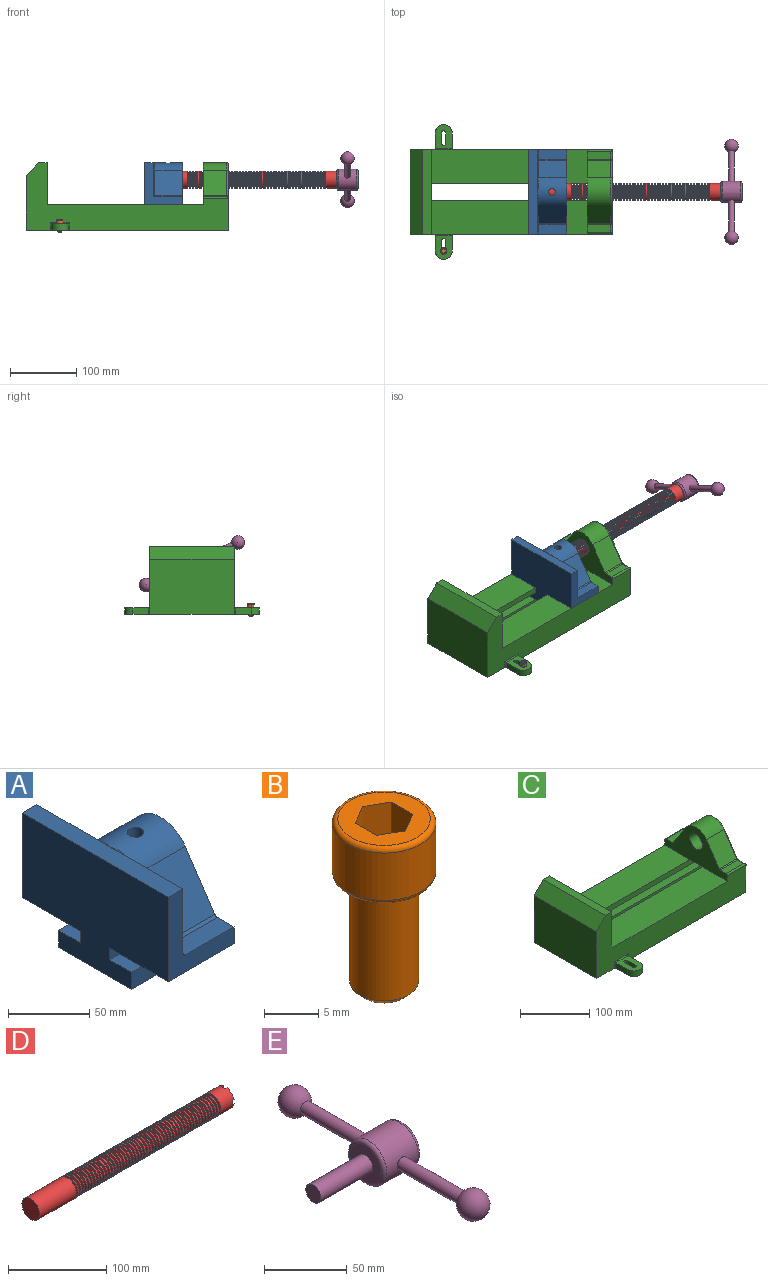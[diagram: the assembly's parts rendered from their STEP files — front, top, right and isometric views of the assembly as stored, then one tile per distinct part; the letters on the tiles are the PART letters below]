
ASSEMBLY  parts=5 mates=5
PART A: 36 faces, bbox 57.2x127x89 mm
  f0: plane 57.15x50.8mm, normal (0,0,-1), area 2903.2mm2, adj f6,f9,f10,f23
  f1: cylinder r=12.7mm len=44.45mm, axis (1,0,0), area 3464.3mm2, adj f6,f15,f16
  f2: plane 41.91x14.52mm, normal (0,0,1), area 608.5mm2, adj f6,f11,f24,f25
  f3: plane 51.86x48.26mm, normal (1,0,0), area 1495.7mm2, adj f8,f10,f31,f33,f35
  f4: plane 51.86x48.26mm, normal (1,0,0), area 1495.7mm2, adj f8,f11,f24,f28,f29
  f5: plane 57.15x50.8mm, normal (0,0,-1), area 2903.2mm2, adj f6,f9,f11,f22
  f6: plane 127x85.09mm, normal (1,0,0), area 5190.6mm2, adj f0,f1,f2,f5,f7,f10,f11,f12
  f7: plane 41.91x14.52mm, normal (0,0,1), area 608.5mm2, adj f6,f10,f30,f31
  f8: plane 127x12.7mm, normal (0,0,1), area 1612.9mm2, adj f3,f4,f9,f10,f11,f26,f34
  f9: plane 127x85.09mm, normal (-1,0,0), area 9096.8mm2, adj f0,f5,f8,f10,f11,f17,f18,f19
  f10: plane 63.5x57.15mm, normal (0,-1,0), area 1372.3mm2, adj f0,f3,f6,f7,f8,f9,f31
  f11: plane 63.5x57.15mm, normal (0,1,0), area 1372.3mm2, adj f2,f4,f5,f6,f8,f9,f24
  f12: plane 41.91x38.43mm, normal (0,-0.83,0.56), area 1939.2mm2, adj f6,f13,f30,f33
  f13: cylinder r=25.4mm len=44.45mm, axis (1,0,0), area 2026.5mm2, adj f6,f12,f14,f16,f26,f28,f34,f35
  f14: plane 41.91x38.43mm, normal (0,0.83,0.56), area 1939.2mm2, adj f6,f13,f25,f29
  f15: plane 25.4x25.4mm, normal (1,0,0), area 506.7mm2, adj f1
  f16: cylinder r=5.08mm len=13.76mm, axis (0,0,1), area 414mm2, adj f1,f13
  f17: plane 57.15x19.05mm, normal (0,0,1), area 1088.7mm2, adj f6,f9,f18,f23
  f18: plane 57.15x12.7mm, normal (0,-1,0), area 725.8mm2, adj f6,f9,f17,f19
  f19: plane 63.5x57.15mm, normal (0,0,-1), area 3629mm2, adj f6,f9,f18,f20
  f20: plane 57.15x12.7mm, normal (0,1,0), area 725.8mm2, adj f6,f9,f19,f21
  f21: plane 57.15x19.05mm, normal (0,0,1), area 1088.7mm2, adj f6,f9,f20,f22
  f22: plane 57.15x8.89mm, normal (0,1,0), area 508.1mm2, adj f5,f6,f9,f21
  f23: plane 57.15x8.89mm, normal (0,-1,0), area 508.1mm2, adj f0,f6,f9,f17
  f24: cylinder r=2.54mm len=14.52mm, axis (0,-1,0), area 57.9mm2, adj f2,f4,f11,f27
  f25: cylinder r=2.54mm len=41.91mm, axis (1,0,0), area 104.3mm2, adj f2,f6,f14,f27
  f26: bspline ~12.24x2.8mm, area 20.9mm2, adj f8,f13,f28
  f27: sphere r=2.54mm, area 6.3mm2, adj f24,f25,f29
  f28: torus R=27.94mm, axis (1,0,0), area 57.8mm2, adj f4,f13,f26,f29
  f29: cylinder r=2.54mm len=39.84mm, axis (0,-0.56,0.83), area 184.6mm2, adj f4,f14,f27,f28
  f30: cylinder r=2.54mm len=41.91mm, axis (1,0,0), area 104.3mm2, adj f6,f7,f12,f32
  f31: cylinder r=2.54mm len=14.52mm, axis (0,-1,0), area 57.9mm2, adj f3,f7,f10,f32
  f32: sphere r=2.54mm, area 6.3mm2, adj f30,f31,f33
  f33: cylinder r=2.54mm len=39.84mm, axis (0,-0.56,-0.83), area 184.6mm2, adj f3,f12,f32,f35
  f34: bspline ~12.24x2.8mm, area 20.9mm2, adj f8,f13,f35
  f35: torus R=27.94mm, axis (1,0,0), area 57.8mm2, adj f3,f13,f33,f34
PART B: 15 faces, bbox 10.3x10.3x19.1 mm
  f0: plane 8.51x8.51mm, normal (0,0,1), area 37.2mm2, adj f5,f6,f7,f8,f9,f10,f14
  f1: cylinder r=3.17mm len=11.94mm, axis (0,0,1), area 238.2mm2, adj f4,f12
  f2: plane 4.83x4.83mm, normal (0,0,-1), area 18.3mm2, adj f12
  f3: cylinder r=4.76mm len=9.53mm, axis (0,0,-1), area 159.6mm2, adj f13,f14
  f4: plane 8.51x8.51mm, normal (0,0,-1), area 25.2mm2, adj f1,f13
  f5: plane 4.83x2.38mm, normal (-0.5,-0.87,0), area 13.3mm2, adj f0,f6,f10,f11
  f6: plane 4.83x2.38mm, normal (0.5,-0.87,0), area 13.3mm2, adj f0,f5,f7,f11
  f7: plane 4.83x2.75mm, normal (1,0,0), area 13.3mm2, adj f0,f6,f8,f11
  f8: plane 4.83x2.38mm, normal (0.5,0.87,0), area 13.3mm2, adj f0,f7,f9,f11
  f9: plane 4.83x2.38mm, normal (-0.5,0.87,0), area 13.3mm2, adj f0,f8,f10,f11
  f10: plane 4.83x2.75mm, normal (-1,0,0), area 13.3mm2, adj f0,f5,f9,f11
  f11: plane 5.5x4.76mm, normal (0,0,1), area 19.6mm2, adj f5,f6,f7,f8,f9,f10
  f12: cone r=3.17mm half-angle=45deg, axis (0,0,1), area 18.9mm2, adj f1,f2
  f13: torus R=4.25mm, axis (0,0,1), area 23mm2, adj f3,f4
  f14: torus R=4.25mm, axis (0,0,1), area 23mm2, adj f0,f3
PART C: 61 faces, bbox 304.8x203.2x103.7 mm
  f0: plane 304.8x101.6mm, normal (0,1,0), area 13520.3mm2, adj f3,f4,f5,f6,f7,f8,f9,f16
  f1: plane 304.8x101.6mm, normal (0,-1,0), area 13520.3mm2, adj f2,f3,f5,f6,f7,f8,f9,f16
  f2: plane 234.95x50.8mm, normal (0,0,1), area 11935.5mm2, adj f1,f5,f16,f26
  f3: plane 127x99.06mm, normal (1,0,0), area 7097.5mm2, adj f0,f1,f9,f14,f17,f18,f19,f20
  f4: plane 234.95x50.8mm, normal (0,0,1), area 11935.5mm2, adj f0,f5,f16,f27
  f5: plane 127x101.6mm, normal (1,0,0), area 9516.1mm2, adj f0,f1,f2,f4,f6,f9,f18,f19
  f6: plane 127x12.7mm, normal (0,0,1), area 1612.9mm2, adj f0,f1,f5,f7
  f7: plane 127x19.05mm, normal (-0.71,0,0.71), area 3421.5mm2, adj f0,f1,f6,f8
  f8: plane 127x82.55mm, normal (-1,0,0), area 10483.8mm2, adj f0,f1,f7,f9
  f9: plane 304.8x203.2mm, normal (0,0,-1), area 33298.3mm2, adj f0,f1,f3,f5,f8,f21,f22,f39
  f10: plane 35.56x11.98mm, normal (0,0,1), area 426mm2, adj f16,f28,f29,f30
  f11: plane 38.43x35.56mm, normal (0,0.83,0.56), area 1645.4mm2, adj f12,f16,f29,f32
  f12: cylinder r=25.4mm len=42.19mm, axis (1,0,0), area 1770.2mm2, adj f11,f13,f16,f33
  f13: plane 38.43x35.56mm, normal (0,-0.83,0.56), area 1645.4mm2, adj f12,f16,f34,f35
  f14: cylinder r=12.7mm len=38.1mm, axis (1,0,0), area 3040.2mm2, adj f3,f16
  f15: plane 35.56x11.98mm, normal (0,0,1), area 426mm2, adj f16,f34,f36,f38
  f16: plane 127x63.5mm, normal (-1,0,0), area 4155.5mm2, adj f0,f1,f2,f4,f10,f11,f12,f13
  f17: plane 38.1x25.4mm, normal (0,0,-1), area 967.7mm2, adj f3,f16,f26,f27
  f18: plane 273.05x19.05mm, normal (0,0,-1), area 5201.6mm2, adj f3,f5,f19,f26
  f19: plane 273.05x12.7mm, normal (0,1,0), area 3467.7mm2, adj f3,f5,f18,f20
  f20: plane 273.05x19.05mm, normal (0,0,1), area 5201.6mm2, adj f3,f5,f19,f21
  f21: plane 273.05x16.51mm, normal (0,1,0), area 4508.1mm2, adj f3,f5,f9,f20
  f22: plane 273.05x16.51mm, normal (0,-1,0), area 4508.1mm2, adj f3,f5,f9,f23
  f23: plane 273.05x19.05mm, normal (0,0,1), area 5201.6mm2, adj f3,f5,f22,f24
  f24: plane 273.05x12.7mm, normal (0,-1,0), area 3467.7mm2, adj f3,f5,f23,f25
  f25: plane 273.05x19.05mm, normal (0,0,-1), area 5201.6mm2, adj f3,f5,f24,f27
  f26: plane 273.05x8.89mm, normal (0,1,0), area 2427.4mm2, adj f2,f3,f5,f17,f18
  f27: plane 273.05x8.89mm, normal (0,-1,0), area 2427.4mm2, adj f3,f4,f5,f17,f25
  f28: cylinder r=2.54mm len=38.1mm, axis (1,0,0), area 148.3mm2, adj f0,f10,f16,f30
  f29: cylinder r=2.54mm len=35.56mm, axis (-1,0,0), area 88.5mm2, adj f10,f11,f16,f31
  f30: cylinder r=2.54mm len=14.52mm, axis (0,1,0), area 54.3mm2, adj f3,f10,f28,f31
  f31: torus R=5.08mm, axis (-1,0,0), area 13.5mm2, adj f3,f29,f30,f32
  f32: cylinder r=2.54mm len=39.84mm, axis (0,0.56,-0.83), area 184.6mm2, adj f3,f11,f31,f33
  f33: torus R=22.86mm, axis (-1,0,0), area 191.4mm2, adj f3,f12,f32,f35
  f34: cylinder r=2.54mm len=35.56mm, axis (-1,0,0), area 88.5mm2, adj f13,f15,f16,f37
  f35: cylinder r=2.54mm len=39.84mm, axis (0,0.56,0.83), area 184.6mm2, adj f3,f13,f33,f37
  f36: cylinder r=2.54mm len=38.1mm, axis (-1,0,0), area 148.3mm2, adj f1,f15,f16,f38
  f37: torus R=5.08mm, axis (-1,0,0), area 13.5mm2, adj f3,f34,f35,f38
  f38: cylinder r=2.54mm len=14.52mm, axis (0,1,0), area 54.3mm2, adj f3,f15,f36,f37
  f39: plane 23.88x9.53mm, normal (-1,0,0), area 227.4mm2, adj f9,f45,f46,f60
  f40: plane 23.88x9.53mm, normal (1,0,0), area 227.4mm2, adj f9,f45,f46,f58
  f41: cylinder r=3.3mm len=9.53mm, axis (0,0,-1), area 98.8mm2, adj f9,f42,f44,f46
  f42: plane 15.62x9.53mm, normal (-1,0,0), area 148.8mm2, adj f9,f41,f43,f46
  f43: cylinder r=3.3mm len=9.53mm, axis (0,0,-1), area 98.8mm2, adj f9,f42,f44,f46
  f44: plane 15.62x9.53mm, normal (1,0,0), area 148.8mm2, adj f9,f41,f43,f46
  f45: cylinder r=12.7mm len=25.4mm, axis (0,0,-1), area 380mm2, adj f9,f39,f40,f46
  f46: plane 36.58x25.4mm, normal (0,0,1), area 722.4mm2, adj f39,f40,f41,f42,f43,f44,f45,f59
  f47: plane 23.88x9.53mm, normal (-1,0,0), area 227.4mm2, adj f9,f53,f54,f56
  f48: plane 23.88x9.53mm, normal (1,0,0), area 227.4mm2, adj f9,f53,f54,f55
  f49: cylinder r=3.3mm len=9.53mm, axis (0,0,-1), area 98.8mm2, adj f9,f50,f52,f54
  f50: plane 15.62x9.53mm, normal (-1,0,0), area 148.8mm2, adj f9,f49,f51,f54
  f51: cylinder r=3.3mm len=9.53mm, axis (0,0,-1), area 98.8mm2, adj f9,f50,f52,f54
  f52: plane 15.62x9.53mm, normal (1,0,0), area 148.8mm2, adj f9,f49,f51,f54
  f53: cylinder r=12.7mm len=25.4mm, axis (0,0,-1), area 380mm2, adj f9,f47,f48,f54
  f54: plane 36.58x25.4mm, normal (0,0,1), area 722.4mm2, adj f47,f48,f49,f50,f51,f52,f53,f57
  f55: cylinder r=1.52mm len=11.05mm, axis (0,0,-1), area 24.1mm2, adj f0,f9,f48,f57
  f56: cylinder r=1.52mm len=11.05mm, axis (0,0,1), area 24.1mm2, adj f0,f9,f47,f57
  f57: cylinder r=1.52mm len=28.45mm, axis (1,0,0), area 63.5mm2, adj f0,f54,f55,f56
  f58: cylinder r=1.52mm len=11.05mm, axis (0,0,1), area 24.1mm2, adj f1,f9,f40,f59
  f59: cylinder r=1.52mm len=28.45mm, axis (-1,0,0), area 63.5mm2, adj f1,f46,f58,f60
  f60: cylinder r=1.52mm len=11.05mm, axis (0,0,-1), area 24.1mm2, adj f1,f9,f39,f59
PART D: 220 faces, bbox 279.4x25.4x25.4 mm
  f0: cylinder r=12.7mm len=25.4mm, axis (-1,0,0), area 1468.2mm2, adj f1,f2,f3,f5,f7,f208,f209,f210
  f1: plane 9.9x9.9mm, normal (1,0,0), area 62.3mm2, adj f0,f4,f213,f216
  f2: plane 9.9x9.9mm, normal (1,0,0), area 62.3mm2, adj f0,f4,f210,f218
  f3: plane 9.9x9.9mm, normal (1,0,0), area 62.3mm2, adj f0,f4,f209,f212
  f4: cylinder r=6.35mm len=25.4mm, axis (1,0,0), area 960.3mm2, adj f1,f2,f3,f5,f6,f208,f209,f210
  f5: plane 9.9x9.9mm, normal (1,0,0), area 62.3mm2, adj f0,f4,f215,f217
  f6: plane 12.7x12.7mm, normal (1,0,0), area 126.7mm2, adj f4
  f7: cone r=12.7mm half-angle=76deg, axis (1,0,0), area 188mm2, adj f0,f9
  f8: cone r=10.16mm half-angle=76deg, axis (-1,0,0), area 188mm2, adj f9,f10
  f9: cylinder r=10.16mm len=20.32mm, axis (1,0,0), area 81.1mm2, adj f7,f8
  f10: cylinder r=12.7mm len=25.4mm, axis (-1,0,0), area 131.7mm2, adj f8,f11
  f11: cone r=12.7mm half-angle=76deg, axis (1,0,0), area 188mm2, adj f10,f13
  f12: cone r=10.16mm half-angle=76deg, axis (-1,0,0), area 188mm2, adj f13,f14
  f13: cylinder r=10.16mm len=20.32mm, axis (1,0,0), area 81.1mm2, adj f11,f12
  f14: cylinder r=12.7mm len=25.4mm, axis (-1,0,0), area 131.7mm2, adj f12,f15
  f15: cone r=12.7mm half-angle=76deg, axis (1,0,0), area 188mm2, adj f14,f17
  f16: cone r=10.16mm half-angle=76deg, axis (-1,0,0), area 188mm2, adj f17,f18
  f17: cylinder r=10.16mm len=20.32mm, axis (1,0,0), area 81.1mm2, adj f15,f16
  f18: cylinder r=12.7mm len=25.4mm, axis (-1,0,0), area 131.7mm2, adj f16,f19
  f19: cone r=12.7mm half-angle=76deg, axis (1,0,0), area 188mm2, adj f18,f21
  f20: cone r=10.16mm half-angle=76deg, axis (-1,0,0), area 188mm2, adj f21,f22
  f21: cylinder r=10.16mm len=20.32mm, axis (1,0,0), area 81.1mm2, adj f19,f20
  f22: cylinder r=12.7mm len=25.4mm, axis (-1,0,0), area 131.7mm2, adj f20,f23
  f23: cone r=12.7mm half-angle=76deg, axis (1,0,0), area 188mm2, adj f22,f25
  f24: cone r=10.16mm half-angle=76deg, axis (-1,0,0), area 188mm2, adj f25,f26
  f25: cylinder r=10.16mm len=20.32mm, axis (1,0,0), area 81.1mm2, adj f23,f24
  f26: cylinder r=12.7mm len=25.4mm, axis (-1,0,0), area 131.7mm2, adj f24,f27
  f27: cone r=12.7mm half-angle=76deg, axis (1,0,0), area 188mm2, adj f26,f29
  f28: cone r=10.16mm half-angle=76deg, axis (-1,0,0), area 188mm2, adj f29,f30
  f29: cylinder r=10.16mm len=20.32mm, axis (1,0,0), area 81.1mm2, adj f27,f28
  f30: cylinder r=12.7mm len=25.4mm, axis (-1,0,0), area 131.7mm2, adj f28,f31
  f31: cone r=12.7mm half-angle=76deg, axis (1,0,0), area 188mm2, adj f30,f33
  f32: cone r=10.16mm half-angle=76deg, axis (-1,0,0), area 188mm2, adj f33,f34
  f33: cylinder r=10.16mm len=20.32mm, axis (1,0,0), area 81.1mm2, adj f31,f32
  f34: cylinder r=12.7mm len=25.4mm, axis (-1,0,0), area 131.7mm2, adj f32,f35
  f35: cone r=12.7mm half-angle=76deg, axis (1,0,0), area 188mm2, adj f34,f37
  f36: cone r=10.16mm half-angle=76deg, axis (-1,0,0), area 188mm2, adj f37,f38
  f37: cylinder r=10.16mm len=20.32mm, axis (1,0,0), area 81.1mm2, adj f35,f36
  f38: cylinder r=12.7mm len=25.4mm, axis (-1,0,0), area 131.7mm2, adj f36,f39
  f39: cone r=12.7mm half-angle=76deg, axis (1,0,0), area 188mm2, adj f38,f41
  f40: cone r=10.16mm half-angle=76deg, axis (-1,0,0), area 188mm2, adj f41,f42
  f41: cylinder r=10.16mm len=20.32mm, axis (1,0,0), area 81.1mm2, adj f39,f40
  f42: cylinder r=12.7mm len=25.4mm, axis (-1,0,0), area 131.7mm2, adj f40,f43
  f43: cone r=12.7mm half-angle=76deg, axis (1,0,0), area 188mm2, adj f42,f45
  f44: cone r=10.16mm half-angle=76deg, axis (-1,0,0), area 188mm2, adj f45,f46
  f45: cylinder r=10.16mm len=20.32mm, axis (1,0,0), area 81.1mm2, adj f43,f44
  f46: cylinder r=12.7mm len=25.4mm, axis (-1,0,0), area 131.7mm2, adj f44,f47
  f47: cone r=12.7mm half-angle=76deg, axis (1,0,0), area 188mm2, adj f46,f49
  f48: cone r=10.16mm half-angle=76deg, axis (-1,0,0), area 188mm2, adj f49,f50
  f49: cylinder r=10.16mm len=20.32mm, axis (1,0,0), area 81.1mm2, adj f47,f48
  f50: cylinder r=12.7mm len=25.4mm, axis (-1,0,0), area 131.7mm2, adj f48,f51
  f51: cone r=12.7mm half-angle=76deg, axis (1,0,0), area 188mm2, adj f50,f53
  f52: cone r=10.16mm half-angle=76deg, axis (-1,0,0), area 188mm2, adj f53,f54
  f53: cylinder r=10.16mm len=20.32mm, axis (1,0,0), area 81.1mm2, adj f51,f52
  f54: cylinder r=12.7mm len=25.4mm, axis (-1,0,0), area 131.7mm2, adj f52,f55
  f55: cone r=12.7mm half-angle=76deg, axis (1,0,0), area 188mm2, adj f54,f57
  f56: cone r=10.16mm half-angle=76deg, axis (-1,0,0), area 188mm2, adj f57,f58
  f57: cylinder r=10.16mm len=20.32mm, axis (1,0,0), area 81.1mm2, adj f55,f56
  f58: cylinder r=12.7mm len=25.4mm, axis (-1,0,0), area 131.7mm2, adj f56,f59
  f59: cone r=12.7mm half-angle=76deg, axis (1,0,0), area 188mm2, adj f58,f61
  f60: cone r=10.16mm half-angle=76deg, axis (-1,0,0), area 188mm2, adj f61,f62
  f61: cylinder r=10.16mm len=20.32mm, axis (1,0,0), area 81.1mm2, adj f59,f60
  f62: cylinder r=12.7mm len=25.4mm, axis (-1,0,0), area 131.7mm2, adj f60,f63
  f63: cone r=12.7mm half-angle=76deg, axis (1,0,0), area 188mm2, adj f62,f65
  f64: cone r=10.16mm half-angle=76deg, axis (-1,0,0), area 188mm2, adj f65,f66
  f65: cylinder r=10.16mm len=20.32mm, axis (1,0,0), area 81.1mm2, adj f63,f64
  f66: cylinder r=12.7mm len=25.4mm, axis (-1,0,0), area 131.7mm2, adj f64,f67
  f67: cone r=12.7mm half-angle=76deg, axis (1,0,0), area 188mm2, adj f66,f69
  f68: cone r=10.16mm half-angle=76deg, axis (-1,0,0), area 188mm2, adj f69,f70
  f69: cylinder r=10.16mm len=20.32mm, axis (1,0,0), area 81.1mm2, adj f67,f68
  f70: cylinder r=12.7mm len=25.4mm, axis (-1,0,0), area 131.7mm2, adj f68,f71
  f71: cone r=12.7mm half-angle=76deg, axis (1,0,0), area 188mm2, adj f70,f73
  f72: cone r=10.16mm half-angle=76deg, axis (-1,0,0), area 188mm2, adj f73,f74
  f73: cylinder r=10.16mm len=20.32mm, axis (1,0,0), area 81.1mm2, adj f71,f72
  f74: cylinder r=12.7mm len=25.4mm, axis (-1,0,0), area 131.7mm2, adj f72,f75
  f75: cone r=12.7mm half-angle=76deg, axis (1,0,0), area 188mm2, adj f74,f77
  f76: cone r=10.16mm half-angle=76deg, axis (-1,0,0), area 188mm2, adj f77,f78
  f77: cylinder r=10.16mm len=20.32mm, axis (1,0,0), area 81.1mm2, adj f75,f76
  f78: cylinder r=12.7mm len=25.4mm, axis (-1,0,0), area 131.7mm2, adj f76,f79
  f79: cone r=12.7mm half-angle=76deg, axis (1,0,0), area 188mm2, adj f78,f81
  f80: cone r=10.16mm half-angle=76deg, axis (-1,0,0), area 188mm2, adj f81,f82
  f81: cylinder r=10.16mm len=20.32mm, axis (1,0,0), area 81.1mm2, adj f79,f80
  f82: cylinder r=12.7mm len=25.4mm, axis (-1,0,0), area 131.7mm2, adj f80,f83
  f83: cone r=12.7mm half-angle=76deg, axis (1,0,0), area 188mm2, adj f82,f85
  f84: cone r=10.16mm half-angle=76deg, axis (-1,0,0), area 188mm2, adj f85,f86
  f85: cylinder r=10.16mm len=20.32mm, axis (1,0,0), area 81.1mm2, adj f83,f84
  f86: cylinder r=12.7mm len=25.4mm, axis (-1,0,0), area 131.7mm2, adj f84,f87
  f87: cone r=12.7mm half-angle=76deg, axis (1,0,0), area 188mm2, adj f86,f89
  f88: cone r=10.16mm half-angle=76deg, axis (-1,0,0), area 188mm2, adj f89,f90
  f89: cylinder r=10.16mm len=20.32mm, axis (1,0,0), area 81.1mm2, adj f87,f88
  f90: cylinder r=12.7mm len=25.4mm, axis (-1,0,0), area 131.7mm2, adj f88,f91
  f91: cone r=12.7mm half-angle=76deg, axis (1,0,0), area 188mm2, adj f90,f93
  f92: cone r=10.16mm half-angle=76deg, axis (-1,0,0), area 188mm2, adj f93,f94
  f93: cylinder r=10.16mm len=20.32mm, axis (1,0,0), area 81.1mm2, adj f91,f92
  f94: cylinder r=12.7mm len=25.4mm, axis (-1,0,0), area 131.7mm2, adj f92,f95
  f95: cone r=12.7mm half-angle=76deg, axis (1,0,0), area 188mm2, adj f94,f97
  f96: cone r=10.16mm half-angle=76deg, axis (-1,0,0), area 188mm2, adj f97,f98
  f97: cylinder r=10.16mm len=20.32mm, axis (1,0,0), area 81.1mm2, adj f95,f96
  f98: cylinder r=12.7mm len=25.4mm, axis (-1,0,0), area 131.7mm2, adj f96,f99
  f99: cone r=12.7mm half-angle=76deg, axis (1,0,0), area 188mm2, adj f98,f101
  f100: cone r=10.16mm half-angle=76deg, axis (-1,0,0), area 188mm2, adj f101,f102
  f101: cylinder r=10.16mm len=20.32mm, axis (1,0,0), area 81.1mm2, adj f99,f100
  f102: cylinder r=12.7mm len=25.4mm, axis (-1,0,0), area 131.7mm2, adj f100,f103
  f103: cone r=12.7mm half-angle=76deg, axis (1,0,0), area 188mm2, adj f102,f105
  f104: cone r=10.16mm half-angle=76deg, axis (-1,0,0), area 188mm2, adj f105,f106
  f105: cylinder r=10.16mm len=20.32mm, axis (1,0,0), area 81.1mm2, adj f103,f104
  f106: cylinder r=12.7mm len=25.4mm, axis (-1,0,0), area 131.7mm2, adj f104,f107
  f107: cone r=12.7mm half-angle=76deg, axis (1,0,0), area 188mm2, adj f106,f109
  f108: cone r=10.16mm half-angle=76deg, axis (-1,0,0), area 188mm2, adj f109,f110
  f109: cylinder r=10.16mm len=20.32mm, axis (1,0,0), area 81.1mm2, adj f107,f108
  f110: cylinder r=12.7mm len=25.4mm, axis (-1,0,0), area 131.7mm2, adj f108,f111
  f111: cone r=12.7mm half-angle=76deg, axis (1,0,0), area 188mm2, adj f110,f113
  f112: cone r=10.16mm half-angle=76deg, axis (-1,0,0), area 188mm2, adj f113,f114
  f113: cylinder r=10.16mm len=20.32mm, axis (1,0,0), area 81.1mm2, adj f111,f112
  f114: cylinder r=12.7mm len=25.4mm, axis (-1,0,0), area 131.7mm2, adj f112,f115
  f115: cone r=12.7mm half-angle=76deg, axis (1,0,0), area 188mm2, adj f114,f117
  f116: cone r=10.16mm half-angle=76deg, axis (-1,0,0), area 188mm2, adj f117,f118
  f117: cylinder r=10.16mm len=20.32mm, axis (1,0,0), area 81.1mm2, adj f115,f116
  f118: cylinder r=12.7mm len=25.4mm, axis (-1,0,0), area 131.7mm2, adj f116,f119
  f119: cone r=12.7mm half-angle=76deg, axis (1,0,0), area 188mm2, adj f118,f121
  f120: cone r=10.16mm half-angle=76deg, axis (-1,0,0), area 188mm2, adj f121,f122
  f121: cylinder r=10.16mm len=20.32mm, axis (1,0,0), area 81.1mm2, adj f119,f120
  f122: cylinder r=12.7mm len=25.4mm, axis (-1,0,0), area 131.7mm2, adj f120,f123
  f123: cone r=12.7mm half-angle=76deg, axis (1,0,0), area 188mm2, adj f122,f125
  f124: cone r=10.16mm half-angle=76deg, axis (-1,0,0), area 188mm2, adj f125,f126
  f125: cylinder r=10.16mm len=20.32mm, axis (1,0,0), area 81.1mm2, adj f123,f124
  f126: cylinder r=12.7mm len=25.4mm, axis (-1,0,0), area 131.7mm2, adj f124,f127
  f127: cone r=12.7mm half-angle=76deg, axis (1,0,0), area 188mm2, adj f126,f129
  f128: cone r=10.16mm half-angle=76deg, axis (-1,0,0), area 188mm2, adj f129,f130
  f129: cylinder r=10.16mm len=20.32mm, axis (1,0,0), area 81.1mm2, adj f127,f128
  f130: cylinder r=12.7mm len=25.4mm, axis (-1,0,0), area 131.7mm2, adj f128,f131
  f131: cone r=12.7mm half-angle=76deg, axis (1,0,0), area 188mm2, adj f130,f133
  f132: cone r=10.16mm half-angle=76deg, axis (-1,0,0), area 188mm2, adj f133,f134
  f133: cylinder r=10.16mm len=20.32mm, axis (1,0,0), area 81.1mm2, adj f131,f132
  f134: cylinder r=12.7mm len=25.4mm, axis (-1,0,0), area 131.7mm2, adj f132,f135
  f135: cone r=12.7mm half-angle=76deg, axis (1,0,0), area 188mm2, adj f134,f137
  f136: cone r=10.16mm half-angle=76deg, axis (-1,0,0), area 188mm2, adj f137,f138
  f137: cylinder r=10.16mm len=20.32mm, axis (1,0,0), area 81.1mm2, adj f135,f136
  f138: cylinder r=12.7mm len=25.4mm, axis (-1,0,0), area 131.7mm2, adj f136,f139
  f139: cone r=12.7mm half-angle=76deg, axis (1,0,0), area 188mm2, adj f138,f141
  f140: cone r=10.16mm half-angle=76deg, axis (-1,0,0), area 188mm2, adj f141,f142
  f141: cylinder r=10.16mm len=20.32mm, axis (1,0,0), area 81.1mm2, adj f139,f140
  f142: cylinder r=12.7mm len=25.4mm, axis (-1,0,0), area 131.7mm2, adj f140,f143
  f143: cone r=12.7mm half-angle=76deg, axis (1,0,0), area 188mm2, adj f142,f145
  f144: cone r=10.16mm half-angle=76deg, axis (-1,0,0), area 188mm2, adj f145,f146
  f145: cylinder r=10.16mm len=20.32mm, axis (1,0,0), area 81.1mm2, adj f143,f144
  f146: cylinder r=12.7mm len=25.4mm, axis (-1,0,0), area 131.7mm2, adj f144,f147
  f147: cone r=12.7mm half-angle=76deg, axis (1,0,0), area 188mm2, adj f146,f149
  f148: cone r=10.16mm half-angle=76deg, axis (-1,0,0), area 188mm2, adj f149,f150
  f149: cylinder r=10.16mm len=20.32mm, axis (1,0,0), area 81.1mm2, adj f147,f148
  f150: cylinder r=12.7mm len=25.4mm, axis (-1,0,0), area 131.7mm2, adj f148,f151
  f151: cone r=12.7mm half-angle=76deg, axis (1,0,0), area 188mm2, adj f150,f153
  f152: cone r=10.16mm half-angle=76deg, axis (-1,0,0), area 188mm2, adj f153,f154
  f153: cylinder r=10.16mm len=20.32mm, axis (1,0,0), area 81.1mm2, adj f151,f152
  f154: cylinder r=12.7mm len=25.4mm, axis (-1,0,0), area 131.7mm2, adj f152,f155
  f155: cone r=12.7mm half-angle=76deg, axis (1,0,0), area 188mm2, adj f154,f157
  f156: cone r=10.16mm half-angle=76deg, axis (-1,0,0), area 188mm2, adj f157,f158
  f157: cylinder r=10.16mm len=20.32mm, axis (1,0,0), area 81.1mm2, adj f155,f156
  f158: cylinder r=12.7mm len=25.4mm, axis (-1,0,0), area 131.7mm2, adj f156,f159
  f159: cone r=12.7mm half-angle=76deg, axis (1,0,0), area 188mm2, adj f158,f161
  f160: cone r=10.16mm half-angle=76deg, axis (-1,0,0), area 188mm2, adj f161,f162
  f161: cylinder r=10.16mm len=20.32mm, axis (1,0,0), area 81.1mm2, adj f159,f160
  f162: cylinder r=12.7mm len=25.4mm, axis (-1,0,0), area 131.7mm2, adj f160,f163
  f163: cone r=12.7mm half-angle=76deg, axis (1,0,0), area 188mm2, adj f162,f165
  f164: cone r=10.16mm half-angle=76deg, axis (-1,0,0), area 188mm2, adj f165,f166
  f165: cylinder r=10.16mm len=20.32mm, axis (1,0,0), area 81.1mm2, adj f163,f164
  f166: cylinder r=12.7mm len=25.4mm, axis (-1,0,0), area 131.7mm2, adj f164,f167
  f167: cone r=12.7mm half-angle=76deg, axis (1,0,0), area 188mm2, adj f166,f169
  f168: cone r=10.16mm half-angle=76deg, axis (-1,0,0), area 188mm2, adj f169,f170
  f169: cylinder r=10.16mm len=20.32mm, axis (1,0,0), area 81.1mm2, adj f167,f168
  f170: cylinder r=12.7mm len=25.4mm, axis (-1,0,0), area 131.7mm2, adj f168,f171
  f171: cone r=12.7mm half-angle=76deg, axis (1,0,0), area 188mm2, adj f170,f173
  f172: cone r=10.16mm half-angle=76deg, axis (-1,0,0), area 188mm2, adj f173,f174
  f173: cylinder r=10.16mm len=20.32mm, axis (1,0,0), area 81.1mm2, adj f171,f172
  f174: cylinder r=12.7mm len=25.4mm, axis (-1,0,0), area 131.7mm2, adj f172,f175
  f175: cone r=12.7mm half-angle=76deg, axis (1,0,0), area 188mm2, adj f174,f177
  f176: cone r=10.16mm half-angle=76deg, axis (-1,0,0), area 188mm2, adj f177,f178
  f177: cylinder r=10.16mm len=20.32mm, axis (1,0,0), area 81.1mm2, adj f175,f176
  f178: cylinder r=12.7mm len=25.4mm, axis (-1,0,0), area 131.7mm2, adj f176,f179
  f179: cone r=12.7mm half-angle=76deg, axis (1,0,0), area 188mm2, adj f178,f181
  f180: cone r=10.16mm half-angle=76deg, axis (-1,0,0), area 188mm2, adj f181,f182
  f181: cylinder r=10.16mm len=20.32mm, axis (1,0,0), area 81.1mm2, adj f179,f180
  f182: cylinder r=12.7mm len=25.4mm, axis (-1,0,0), area 131.7mm2, adj f180,f183
  f183: cone r=12.7mm half-angle=76deg, axis (1,0,0), area 188mm2, adj f182,f185
  f184: cone r=10.16mm half-angle=76deg, axis (-1,0,0), area 188mm2, adj f185,f186
  f185: cylinder r=10.16mm len=20.32mm, axis (1,0,0), area 81.1mm2, adj f183,f184
  f186: cylinder r=12.7mm len=25.4mm, axis (-1,0,0), area 131.7mm2, adj f184,f187
  f187: cone r=12.7mm half-angle=76deg, axis (1,0,0), area 188mm2, adj f186,f189
  f188: cone r=10.16mm half-angle=76deg, axis (-1,0,0), area 188mm2, adj f189,f190
  f189: cylinder r=10.16mm len=20.32mm, axis (1,0,0), area 81.1mm2, adj f187,f188
  f190: cylinder r=12.7mm len=25.4mm, axis (-1,0,0), area 131.7mm2, adj f188,f191
  f191: cone r=12.7mm half-angle=76deg, axis (1,0,0), area 188mm2, adj f190,f193
  f192: cone r=10.16mm half-angle=76deg, axis (-1,0,0), area 188mm2, adj f193,f194
  f193: cylinder r=10.16mm len=20.32mm, axis (1,0,0), area 81.1mm2, adj f191,f192
  f194: cylinder r=12.7mm len=25.4mm, axis (-1,0,0), area 131.7mm2, adj f192,f195
  f195: cone r=12.7mm half-angle=76deg, axis (1,0,0), area 188mm2, adj f194,f197
  f196: cone r=10.16mm half-angle=76deg, axis (-1,0,0), area 188mm2, adj f197,f198
  f197: cylinder r=10.16mm len=20.32mm, axis (1,0,0), area 81.1mm2, adj f195,f196
  f198: cylinder r=12.7mm len=25.4mm, axis (-1,0,0), area 131.7mm2, adj f196,f199
  f199: cone r=12.7mm half-angle=76deg, axis (1,0,0), area 188mm2, adj f198,f201
  f200: cone r=10.16mm half-angle=76deg, axis (-1,0,0), area 188mm2, adj f201,f202
  f201: cylinder r=10.16mm len=20.32mm, axis (1,0,0), area 81.1mm2, adj f199,f200
  f202: cylinder r=12.7mm len=25.4mm, axis (-1,0,0), area 131.7mm2, adj f200,f203
  f203: cone r=12.7mm half-angle=76deg, axis (1,0,0), area 188mm2, adj f202,f205
  f204: cone r=10.16mm half-angle=76deg, axis (-1,0,0), area 188mm2, adj f205,f207
  f205: cylinder r=10.16mm len=20.32mm, axis (1,0,0), area 81.1mm2, adj f203,f204
  f206: plane 25.4x25.4mm, normal (-1,0,0), area 506.7mm2, adj f207
  f207: cylinder r=12.7mm len=52.45mm, axis (-1,0,0), area 4185.4mm2, adj f204,f206
  f208: plane 6.88x5.08mm, normal (1,0,0), area 32.7mm2, adj f0,f4,f209,f210
  f209: plane 6.62x2.54mm, normal (0,-1,0), area 16.8mm2, adj f0,f3,f4,f208
  f210: plane 6.62x2.54mm, normal (0,1,0), area 16.8mm2, adj f0,f2,f4,f208
  f211: plane 6.88x5.08mm, normal (1,0,0), area 32.7mm2, adj f0,f4,f212,f213
  f212: plane 6.62x2.54mm, normal (0,0,1), area 16.8mm2, adj f0,f3,f4,f211
  f213: plane 6.62x2.54mm, normal (0,0,-1), area 16.8mm2, adj f0,f1,f4,f211
  f214: plane 6.88x5.08mm, normal (1,0,0), area 32.7mm2, adj f0,f4,f215,f216
  f215: plane 6.62x2.54mm, normal (0,1,0), area 16.8mm2, adj f0,f4,f5,f214
  f216: plane 6.62x2.54mm, normal (0,-1,0), area 16.8mm2, adj f0,f1,f4,f214
  f217: plane 6.62x2.54mm, normal (0,0,-1), area 16.8mm2, adj f0,f4,f5,f219
  f218: plane 6.62x2.54mm, normal (0,0,1), area 16.8mm2, adj f0,f2,f4,f219
  f219: plane 6.88x5.08mm, normal (1,0,0), area 32.7mm2, adj f0,f4,f217,f218
PART E: 11 faces, bbox 76.2x172.7x34.4 mm
  f0: sphere r=10.16mm, area 1231.8mm2, adj f1
  f1: cylinder r=4.45mm len=51.82mm, axis (0,1,0), area 1438.5mm2, adj f0,f4
  f2: sphere r=10.16mm, area 1231.8mm2, adj f3
  f3: cylinder r=4.45mm len=51.82mm, axis (0,1,0), area 1438.5mm2, adj f2,f4
  f4: cylinder r=15.88mm len=31.75mm, axis (-1,0,0), area 2534.7mm2, adj f1,f3,f9,f10
  f5: cylinder r=6.35mm len=44.45mm, axis (-1,0,0), area 1773.5mm2, adj f6,f8
  f6: plane 12.7x12.7mm, normal (-1,0,0), area 126.7mm2, adj f5
  f7: plane 26.67x26.67mm, normal (1,0,0), area 558.6mm2, adj f10
  f8: plane 26.67x26.67mm, normal (-1,0,0), area 432mm2, adj f5,f9
  f9: torus R=13.33mm, axis (1,0,0), area 374.8mm2, adj f4,f8
  f10: torus R=13.33mm, axis (1,0,0), area 374.8mm2, adj f4,f7
PLACE A t=(146.93,0,0)mm
PLACE B rot(axis=(0,0,1),90deg) t=(-254,-88.9,9.52)mm
PLACE C at identity fixed
PLACE D rot(axis=(-1,0,0),24.9deg) t=(146.93,-32.05,7.07)mm
PLACE E rot(axis=(-1,0,0),24.9deg) t=(125.34,-32.05,7.07)mm
MATE fastened D.f4 <-> E.f5  axis (1,0,0) through (163.44,0,76.2)mm
MATE planar A.f0 <-> C.f2  axis (0,0,-1) through (-97.55,-38.1,38.1)mm
MATE pin_slot B.f1 <-> C.f41  axis (0,0,1) through (-254,-88.9,9.52)mm
MATE revolute D.f7 <-> A.f28  axis (-1,0,0) through (-113.42,0,76.2)mm
MATE cylindrical C.f12 <-> D.f7  axis (-1,0,0) through (-38.1,0,76.2)mm
